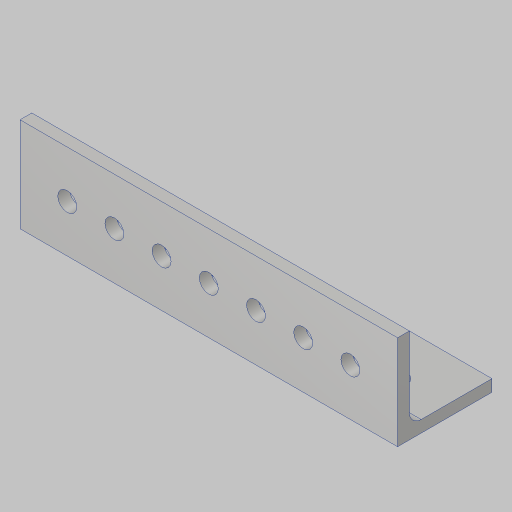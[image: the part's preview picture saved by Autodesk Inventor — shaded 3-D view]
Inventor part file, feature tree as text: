
AUTODESK INVENTOR PART (.ipt)
format: ipt  version: 2023.5 (Build 275446000, 446)  size: 139,776 bytes
history: native  units: in
note: dims shown in document units (in); Inventor stores cm internally (conversion verified against a paired STEP export)
features: sketch x3, hole x2, extrude x1, fillet x1
ambient origin geometry x8: Origin, YZ Plane, XZ Plane, XY Plane, X Axis, Y Axis, Z Axis, Center Point
bodies: Solid1 (feature_tree)
feature tree (7):
  extrude  "Extrusion1"  Depth=1.0in
  fillet  "Fillet1"  Radius=0.125in
  hole  "Hole1"  [1 undecoded]
  hole  "Hole2"  [1 undecoded]
  sketch  "Sketch1"  dims[d0=1.0in d1=1.0in d2=0.125in]
  sketch  "Sketch2"  dims[d3=4.0in d4=0.0in d5=0.125in]
  sketch  "Sketch3"  dims[d6=0.5in d7=2.7559in d9=0.5in d10=0.3937in d12=1.0in d14=0.201in d15=0.75in d16=0.385in d17=0.25in d18=0.5635in d19=1.0in d20=0.8108in d21=0.5in d22=2.7559in d24=0.5in d25=0.3937in d27=1.0in d29=0.201in d30=0.75in d31=0.375in d32=0.25in d33=0.5635in d34=1.0in d35=0.8108in]
note: 2 required parameter values undecoded (feature->parameter linkage not recoverable at this tier; creation-order binding heuristic only, values carry confidence <= 0.55)
